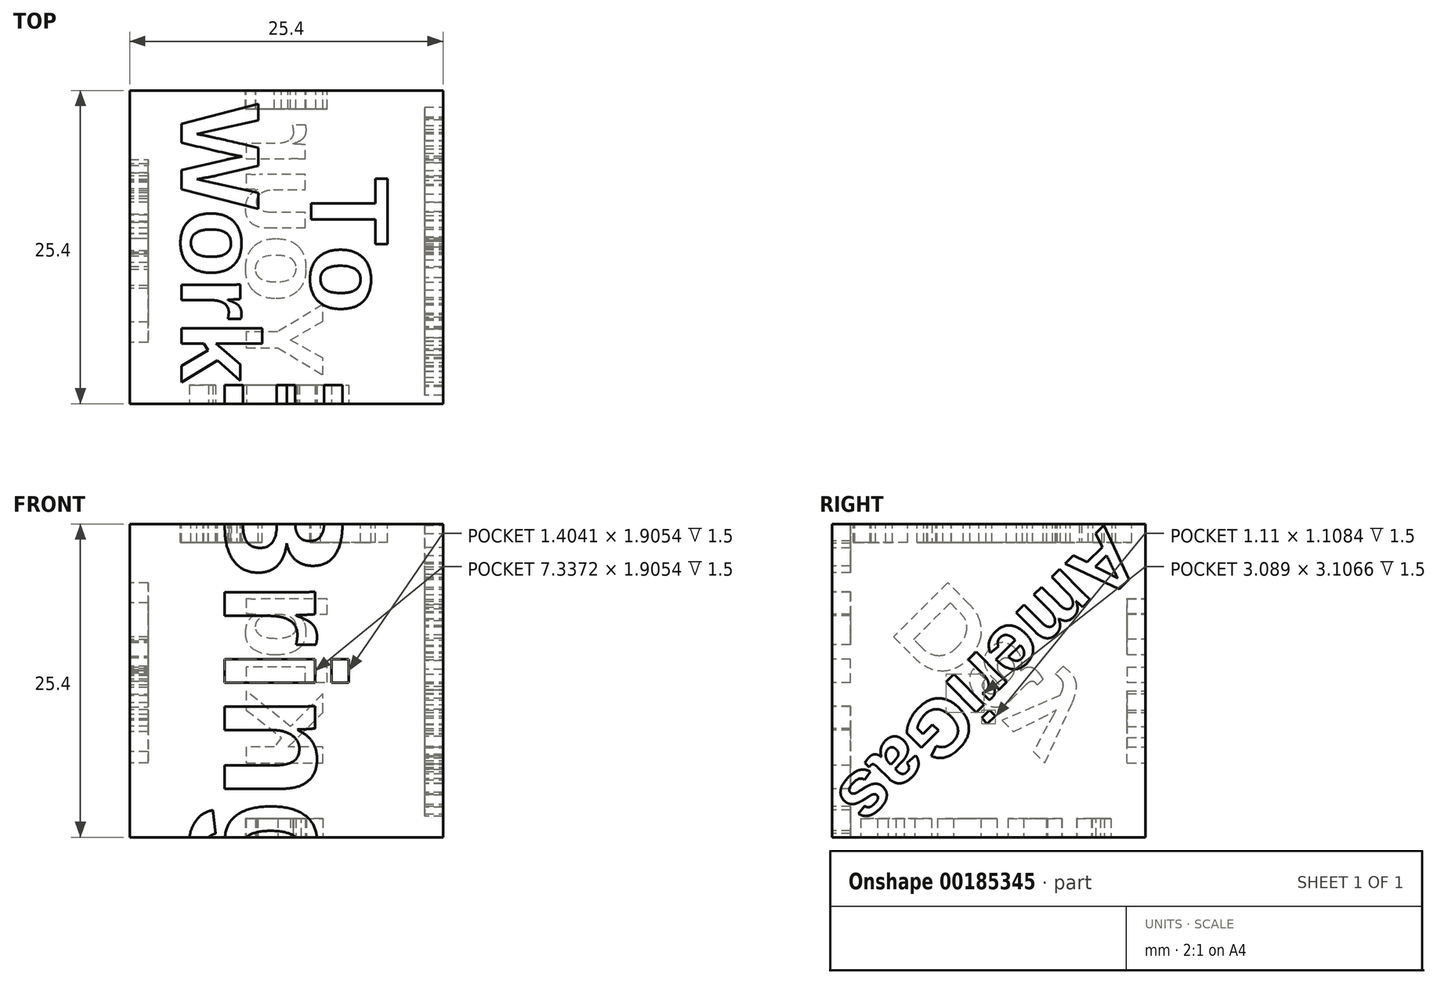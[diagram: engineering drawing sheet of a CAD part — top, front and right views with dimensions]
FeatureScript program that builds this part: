
annotation { "Feature Type Name" : "Feature", "Feature Type Description" : "" }
export const myFeature = defineFeature(function(context is Context, id is Id, definition is map)
    precondition{}
    {
        {
            assignVariable(context, id + "F0", {"name" : "textextruded", "anyValue" : 1.5});
        }
        {
            var Q0;
            Q0=qCreatedBy(makeId("Front.planeOp"),FACE);
            var sketch = newSketch(context, id + "F1", { "sketchPlane" : qUnion([Q0])});
            skLineSegment(sketch, "E0.bottom", {"start": v(12.7, 12.7) * mm, "end": v(-12.7, 12.7) * mm});
            skLineSegment(sketch, "E0.top", {"start": v(12.7, -12.7) * mm, "end": v(-12.7, -12.7) * mm});
            skLineSegment(sketch, "E0.left", {"start": v(12.7, 12.7) * mm, "end": v(12.7, -12.7) * mm});
            skLineSegment(sketch, "E0.right", {"start": v(-12.7, 12.7) * mm, "end": v(-12.7, -12.7) * mm});
            skPoint(sketch, "E0.middle", {"position": v(0, 0) * mm});
            skSolve(sketch);
        }
        {
            var Q0;
            Q0 = qSketchRegion(id + "F1", true);
            extrude(context, id + "F2", {"entities" : qUnion([Q0]), "depth" : 25.4 * mm, "offsetDistance" : 25 * mm, "symmetric" : true});
        }
        {
            var Q0;
            Q0=makeQuery(id+"F2.opExtrude","SWEPT_FACE",FACE,{"disambiguationData":[OSD([sQuery(id+"F1.wireOp",EDGE,"E0.bottom")])]});
            var sketch = newSketch(context, id + "F3", { "sketchPlane" : qUnion([Q0])});
            skText(sketch, "E1", { "text": "AmeriGas", "fontName": "Arimo-Bold.ttf"});
            skPoint(sketch, "E2", {"position": v(0, 0) * mm});
            const initialGuessF3  = {"E1": [-0.0127, 0.00945, 0.70368, -0.71052, 0.00474]};
            skSetInitialGuess(sketch, initialGuessF3);
            skSolve(sketch);
        }
        {
            var Q0;
            Q0 = qSketchRegion(id + "F3", true);
            extrude(context, id + "F4", {"entities" : qUnion([Q0]), "operationType" : NewBodyOperationType.REMOVE, "oppositeDirection" : true, "depth" : (getVariable(context, 'textextruded')) * mm, "offsetDistance" : 25 * mm});
        }
        {
            var Q0;
            Q0=makeQuery(id+"F2.opExtrude","CAP_FACE",FACE,{"disambiguationData":[OSD([sQuery(id+"F1.wireOp",EDGE,"E0.bottom"),sQuery(id+"F1.wireOp",EDGE,"E0.top"),sQuery(id+"F1.wireOp",EDGE,"E0.left"),sQuery(id+"F1.wireOp",EDGE,"E0.right")])],"isStart":false});
            var sketch = newSketch(context, id + "F5", { "sketchPlane" : qUnion([Q0])});
            skText(sketch, "E3", { "text": "Bring", "fontName": "Arimo-Bold.ttf"});
            skPoint(sketch, "E4", {"position": v(0, 0) * mm});
            const initialGuessF5  = {"E3": [-0.01815, -0.005, 1, 0, 0.01]};
            skSetInitialGuess(sketch, initialGuessF5);
            skSolve(sketch);
        }
        {
            var Q0;
            Q0 = qSketchRegion(id + "F5", true);
            extrude(context, id + "F6", {"entities" : qUnion([Q0]), "operationType" : NewBodyOperationType.REMOVE, "oppositeDirection" : true, "depth" : (getVariable(context, 'textextruded')) * mm, "offsetDistance" : 25 * mm});
        }
        {
            var Q0;
            Q0=makeQuery(id+"F2.opExtrude","SWEPT_FACE",FACE,{"disambiguationData":[OSD([sQuery(id+"F1.wireOp",EDGE,"E0.left")])]});
            var sketch = newSketch(context, id + "F7", { "sketchPlane" : qUnion([Q0])});
            skText(sketch, "E5", { "text": "Your", "fontName": "Arimo-Bold.ttf"});
            skPoint(sketch, "E6", {"position": v(0, 0) * mm});
            const initialGuessF7  = {"E5": [-0.01053, -0.00325, 1, 0, 0.0065]};
            skSetInitialGuess(sketch, initialGuessF7);
            skSolve(sketch);
        }
        {
            var Q0;
            Q0=makeQuery(id+"F2.opExtrude","CAP_FACE",FACE,{"disambiguationData":[OSD([sQuery(id+"F1.wireOp",EDGE,"E0.bottom"),sQuery(id+"F1.wireOp",EDGE,"E0.top"),sQuery(id+"F1.wireOp",EDGE,"E0.left"),sQuery(id+"F1.wireOp",EDGE,"E0.right")])],"isStart":true});
            var sketch = newSketch(context, id + "F8", { "sketchPlane" : qUnion([Q0])});
            skText(sketch, "E7", { "text": "Kid", "fontName": "Arimo-Bold.ttf"});
            skPoint(sketch, "E8", {"position": v(0, 0) * mm});
            const initialGuessF8  = {"E7": [-0.00729, -0.00325, 1, 0, 0.0065]};
            skSetInitialGuess(sketch, initialGuessF8);
            skSolve(sketch);
        }
        {
            var Q0;
            Q0=makeQuery(id+"F2.opExtrude","SWEPT_FACE",FACE,{"disambiguationData":[OSD([sQuery(id+"F1.wireOp",EDGE,"E0.right")])]});
            var sketch = newSketch(context, id + "F9", { "sketchPlane" : qUnion([Q0])});
            skText(sketch, "E9", { "text": "To", "fontName": "Arimo-Bold.ttf"});
            skPoint(sketch, "E10", {"position": v(0, 5.25) * mm});
            skText(sketch, "E11", { "text": "Work", "fontName": "Arimo-Bold.ttf"});
            skPoint(sketch, "E12", {"position": v(0, -5.25) * mm});
            skLineSegment(sketch, "E13", {"start": v(-5.65, 8.5) * mm, "end": v(11.6, -8.5) * mm, "construction": true});
            skPoint(sketch, "E14", {"position": v(2.98, 0) * mm});
            const initialGuessF9  = {"E9": [-0.00565, 0.002, 1, 0, 0.0065], "E11": [-0.0116, -0.0085, 1, 0, 0.0065]};
            skSetInitialGuess(sketch, initialGuessF9);
            skSolve(sketch);
        }
        {
            var Q0;
            Q0=makeQuery(id+"F2.opExtrude","SWEPT_FACE",FACE,{"disambiguationData":[OSD([sQuery(id+"F1.wireOp",EDGE,"E0.top")])]});
            var sketch = newSketch(context, id + "F10", { "sketchPlane" : qUnion([Q0])});
            skText(sketch, "E15", { "text": "Day", "fontName": "Arimo-Bold.ttf"});
            skPoint(sketch, "E16", {"position": v(0, 0) * mm});
            const initialGuessF10  = {"E15": [-0.00836, 0.00376, 0.7071, -0.7071, 0.0065]};
            skSetInitialGuess(sketch, initialGuessF10);
            skSolve(sketch);
        }
        {
            var Q0;
            Q0 = qSketchRegion(id + "F7", true);
            extrude(context, id + "F11", {"entities" : qUnion([Q0]), "operationType" : NewBodyOperationType.REMOVE, "oppositeDirection" : true, "depth" : (getVariable(context, 'textextruded')) * mm, "offsetDistance" : 25 * mm});
        }
        {
            var Q0;
            Q0 = qSketchRegion(id + "F9", true);
            extrude(context, id + "F12", {"entities" : qUnion([Q0]), "operationType" : NewBodyOperationType.REMOVE, "oppositeDirection" : true, "depth" : (getVariable(context, 'textextruded')) * mm, "offsetDistance" : 25 * mm});
        }
        {
            var Q0;
            Q0 = qSketchRegion(id + "F8", true);
            extrude(context, id + "F13", {"entities" : qUnion([Q0]), "operationType" : NewBodyOperationType.REMOVE, "oppositeDirection" : true, "depth" : (getVariable(context, 'textextruded')) * mm, "offsetDistance" : 25 * mm});
        }
        {
            var Q0;
            Q0 = qSketchRegion(id + "F10", true);
            extrude(context, id + "F14", {"entities" : qUnion([Q0]), "operationType" : NewBodyOperationType.REMOVE, "oppositeDirection" : true, "depth" : (getVariable(context, 'textextruded')) * mm, "offsetDistance" : 25 * mm});
        }
        {
            var Q0;
            Q0=makeQuery(id+"F2.opExtrude","SWEPT_BODY",BODY,{"disambiguationData":[OSD([sQuery(id+"F1.wireOp",EDGE,"E0.bottom"),sQuery(id+"F1.wireOp",EDGE,"E0.top"),sQuery(id+"F1.wireOp",EDGE,"E0.left"),sQuery(id+"F1.wireOp",EDGE,"E0.right")])]});
            var Q1;
            Q1=makeQuery(id+"F2.opExtrude","SWEPT_EDGE",EDGE,{"disambiguationData":[OSD([sQuery(id+"F1.wireOp",EDGE,"E0.top"),sQuery(id+"F1.wireOp",EDGE,"E0.left")])]});
            transform(context, id + "F15", {"entities" : qUnion([Q0]), "transformType" : TransformType.ROTATION, "transformAxis" : qUnion([Q1]), "angle" : 90 * degree, "makeCopy" : false});
        }
    });
